# Revit family: 0047805 Feilo Sylvania Lighting Fixtures START WATERPROOF LED 1565MM T CW 6500LM
name_source: partatom
category: Lighting Fixtures
revit_build: Autodesk Revit 2017 (Build: 20190507_1515(x64)
units: mm (PartAtom-declared; Revit-internal decimal feet)

## family parameters
Cut with Voids When Loaded = No
Host = Face
Light Source = Yes
OmniClass Number = 23.80.70.11.17
OmniClass Title = Specialized Lighting by Location or Use
Part Type = Normal
Room Calculation Point = No
Round Connector Dimension = Use Diameter
Shared = No

## types (1)
- START WATERPROOF LED 1565MM T CW 6500LM
    Apparent Load = 60 VA
    Assembly Code = D5020200
    AssetType = Fixed
    Body Material = Polycarbonate_Body_Sylvania_Brite White
    Bracket-Diffuser Material = <By Category>
    Bracket-Mounting Material = <By Category>
    Color Filter = 16777215
    Default Elevation = 0 mm  [stored 0 ft]
    Description = Weather resistant LED Luminaire, 1565MM with Twin Lamp, 60W at 6500K, 108lm/W. UV stablised polycarbonate cover with specially designed opal lens - softens and control the light whilst optimising output.  No yellow staining. Highly efficient electronic driver included as standard. Smooth body finish, easy to handle. Minimal maintainence with no replacement of lamps . Through wiring achievable. IP65 rating and IK08 body durable for harsh locations. Professionally finished with Stainless Steel brackets. Suspension compatible.
    Diffuser Material = Polycarbonate_Diffuser_Sylvania_Clear
    DiffuserBracketsLength_FEILO = 1405 mm  [stored 4.60958 ft]
    Dimming Lamp Color Temperature Shift = <None>
    DimmingControlOptions = Non dimmable
    DocumentationLiterature = http://www.sylvania-lighting.com
    DurationUnit = hours
    ElectricShockClassification = Class I
    Emit Shape Visible in Rendering = No
    Emit from Rectangle Length = 1545 mm
    Emit from Rectangle Width = 95 mm  [stored 0.31168 ft]
    ExpectedLife = 50000
    Height_FEILO = 91 mm  [stored 0.298556 ft]
    IfcExportAs = IfcLightFixtureType
    IfcExportType = IfcLightFixtureType
    ImpactProtectionIndex = IK08
    IngressProtection = IP65
    InputVoltage = 220-240V~
    Keynote = 16500
    Lamp = LED
    Lamp Material = Acrylic High Luminance Glass_Lamp_Sylvania_White
    LampColourRenderingIndex = 80
    LampColourTemperature = 6500 K
    LampNominalLuminous = 6500 lm
    LampSingle_FEILO = No
    LampTwin_FEILO = Yes
    LampsType = LED
    LengthHelp_FEILO = 1505 mm  [stored 4.93766 ft]
    Length_FEILO = 1565 mm
    LightOutputRatio = 100
    LuminousEfficacy = 108.33 lm/W
    Manufacturer = Feilo Sylvania
    ManufacturerName = Feilo Sylvania
    Material = polycarbonate housing, polycarbonate diffuser
    Model = START WATERPROOF LED 1265MM SINGLE 4000K
    ModelNumber = 0047805
    ModelReference = START WATERPROOF LED 1565MM T CW 6500LM
    MountingBracketsLength_FEILO = 955 mm  [stored 3.1332 ft]
    MountingBracketsWidth_FEILO = 54 mm  [stored 0.177165 ft]
    Name = START WATERPROOF LED 1565MM T CW 6500LM
    NominalHeight = 91 mm  [stored 0.298556 ft]
    NominalLength = 1565 mm
    NominalWidth = 0 mm  [stored 0 ft]
    NumberOfDiffuserBrackets_FEILO = 3
    Photometric Web File = 0047805.ies
    PowerConsumption = 60 W
    PowerFactor = 0
    SideVoidWidth_FEILO = 70 mm
    Tilt Angle = -90.00°
    TypeName = START WATERPROOF LED 1565MM T CW 6500LM
    URL = http://www.sylvania-lighting.com
    Voltage = 230 V
    Weight = 2.58 kg
    WidthHelp_FEILO = 55 mm
    Width_FEILO = 123 mm

note: [stored X ft] marks values corroborated as IEEE doubles in the binary element streams (Revit-internal decimal feet)

## geometry (parser evidence)
native form markers: Sweep x12
no freeform markers — native parametric forms only
